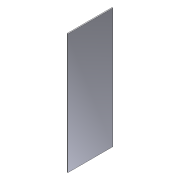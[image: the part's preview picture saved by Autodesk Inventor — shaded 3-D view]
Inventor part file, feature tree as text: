
AUTODESK INVENTOR PART (.ipt)
format: ipt  version: 2012 (Build 160160000, 160)  size: 68,608 bytes
history: native  units: in
note: dims shown in document units (in); Inventor stores cm internally (conversion verified against a paired STEP export)
features: extrude x1, sketch x1
ambient origin geometry x8: Origin, YZ Plane, XZ Plane, XY Plane, X Axis, Y Axis, Z Axis, Center Point
bodies: Solid1 (feature_tree)
feature tree (2):
  extrude  "Extrusion1"  Depth=16.0in
  sketch  "Sketch1"  dims[d0=0.125in d1=16.0in d2=6.0in d3=0.0in]
